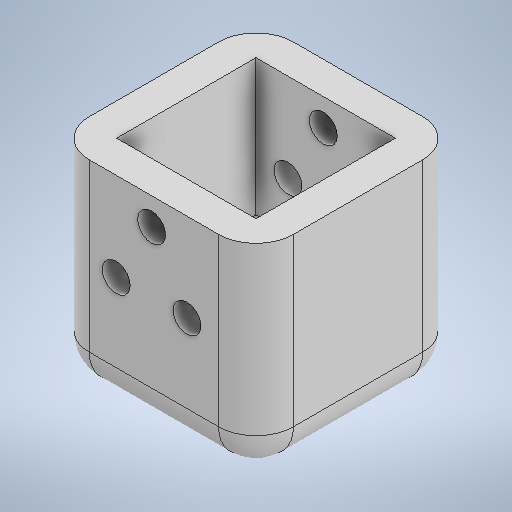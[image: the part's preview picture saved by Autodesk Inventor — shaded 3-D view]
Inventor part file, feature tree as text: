
AUTODESK INVENTOR PART (.ipt)
format: ipt  version: 2025 (Build 290162000, 162)  size: 295,424 bytes
history: native  units: mm
features: sketch x6, extrude x4, revolve x1, fillet x1
ambient origin geometry x8: Origin, YZ Plane, XZ Plane, XY Plane, X Axis, Y Axis, Z Axis, Center Point
bodies: Solid1 (feature_tree)
feature tree (12):
  extrude  "Extrusion1"  Depth=20.5mm
  extrude  "Extrusion2"  Depth=30.0mm
  extrude  "Extrusion3"  TaperAngle=0.0deg  [1 undecoded]
  revolve  "Revolution1"  [1 undecoded]
  extrude  "Extrusion4"  Depth=24.9mm TaperAngle=0.0deg
  fillet  "Fillet2"  Radius=30.0mm
  sketch  "Sketch2"  dims[d4=30.0mm d5=30.0mm]
  sketch  "Sketch3"  dims[d6=20.0mm d7=0.0mm]
  sketch  "Sketch Circular Pattern1"  dims[d2=20.5mm d3=20.5mm]
  sketch  "Sketch4"  dims[d8=4.1mm d9=6.0mm]
  sketch  "Sketch5"  dims[d10=30.0mm d12=360.0deg d14=24.9mm d15=0.0mm d16=30.0mm]
  sketch  "Sketch6"  dims[d17=30.0mm d18=25.0mm d19=0.0mm d20=40.0mm d21=90.0deg d23=45.0mm d24=45.0mm d25=15.0mm d26=0.0mm d27=5.5mm]
note: 2 required parameter values undecoded (feature->parameter linkage not recoverable at this tier; creation-order binding heuristic only, values carry confidence <= 0.55)